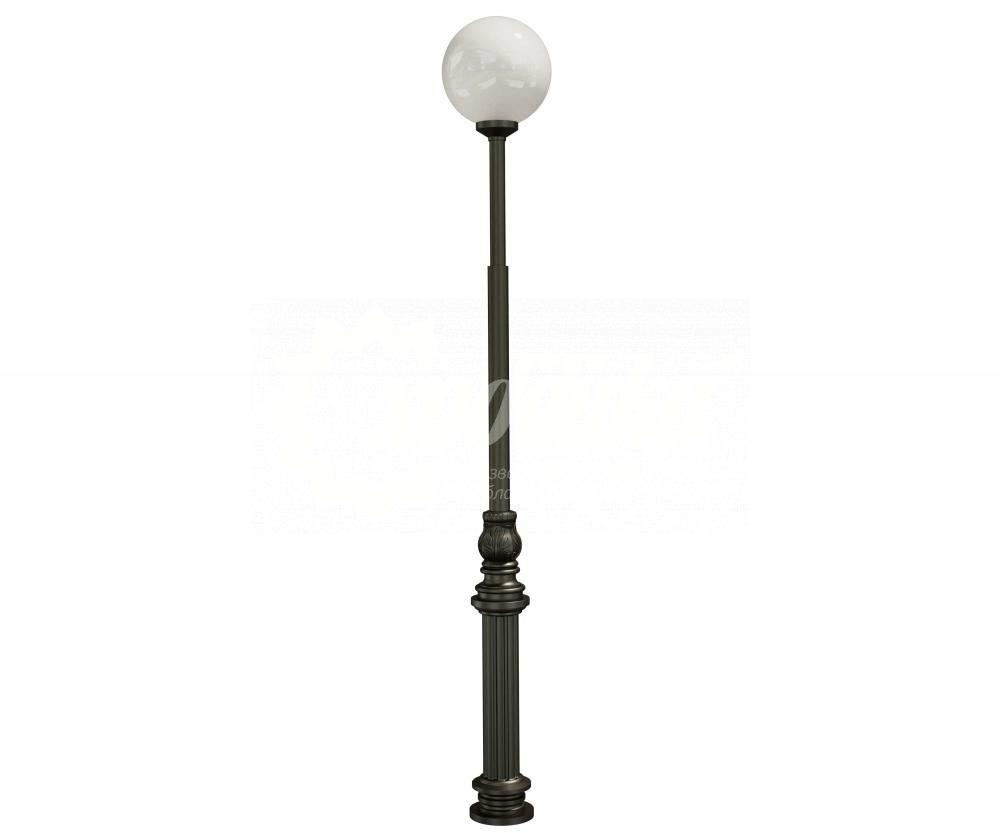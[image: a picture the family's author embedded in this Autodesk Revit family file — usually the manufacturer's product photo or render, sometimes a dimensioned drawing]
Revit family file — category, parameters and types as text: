
# Revit family: Фонарный столб А-03 со светильником Арт 7415
name_source: partatom
category: Антураж
revit_build: Autodesk Revit 2018 (Build: 20180423_1000(x64)
units: mm (PartAtom-declared; Revit-internal decimal feet)

## family parameters
Всегда вертикально = Да
Источник визуального образа = Геометрия семейства
На основе рабочей плоскости = Нет
Общий = Нет
При загрузке вырезать с полостями = Нет
Точка расчета площади = Нет

## types (6) — shared parameters
URL = https://hobbyka.ru
Артикул товара = Арт. 7415
Группа модели = Светильники с чугунными опорами
Длина = 400 мм
Изготовитель = ООО «Хоббика»
Изображение типоразмера = Фонарный столб А-03 со светильником Арт 7415.jpg
Материал изделия = Сталь
Цвет каркаса = Сталь
Ширина = 400 мм

## per-type parameters (varying)
| type | Версия 2,911 м | Версия 3,411 м | Версия 3,911 м | Версия 4,411 м | Версия 4,911 м | Высота | Высота столба | Описание |
| Версия 2,911 м | Да | Нет | Нет | Нет | Нет | 2911 мм | 1970 мм | Фонарный столб А-03 со светильником. Версия 2,911 м |
| Версия 3,411 м | Нет | Да | Нет | Нет | Нет | 3411 мм | 2470 мм | Фонарный столб А-03 со светильником. Версия 3,411 м |
| Версия 3,911 м | Нет | Нет | Да | Нет | Нет | 3911 мм | 2970 мм | Фонарный столб А-03 со светильником. Версия 3,911 м |
| Версия 4,411 м | Нет | Нет | Нет | Да | Нет | 4411 мм | 3470 мм | Фонарный столб А-03 со светильником. Версия 4,411 м |
| Версия 4,911 м | Нет | Нет | Нет | Нет | Да | 4911 мм | 3970 мм | Фонарный столб А-03 со светильником. Версия 4,911 м |
| Версия 5,411 м | Нет | Нет | Нет | Нет | Нет | 5411 мм | 4470 мм | Фонарный столб А-03 со светильником. Версия 5,411 м |
